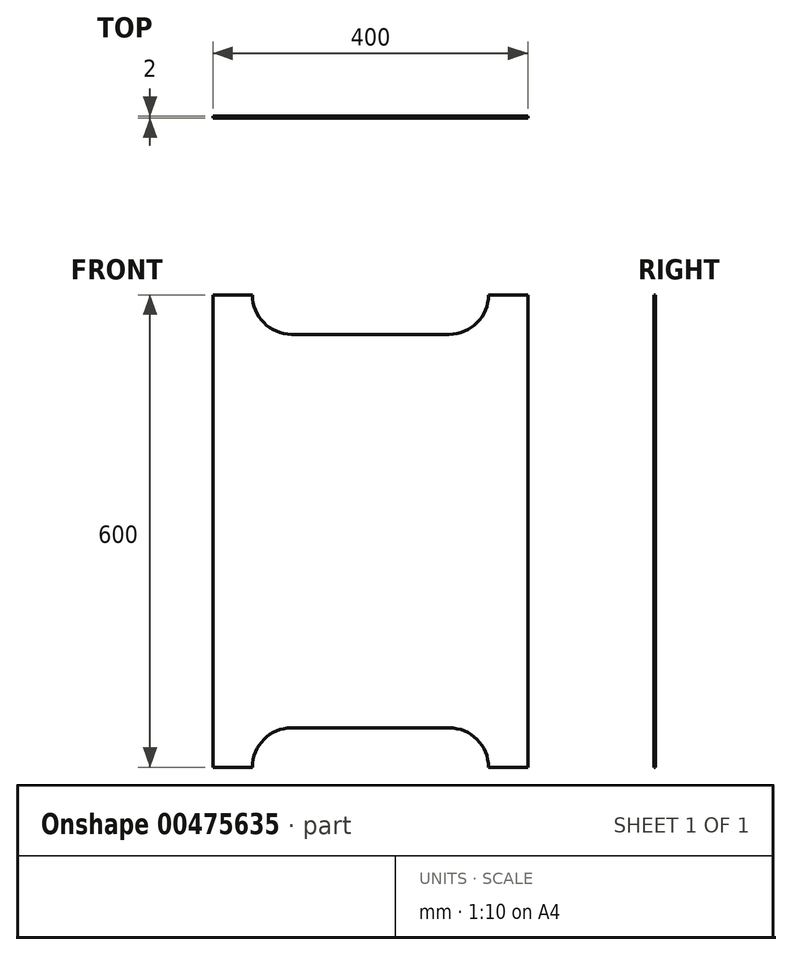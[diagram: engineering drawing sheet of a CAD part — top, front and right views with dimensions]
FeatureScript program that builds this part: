
annotation { "Feature Type Name" : "Feature", "Feature Type Description" : "" }
export const myFeature = defineFeature(function(context is Context, id is Id, definition is map)
    precondition{}
    {
        {
            var Q0;
            Q0=qCreatedBy(makeId("Front.planeOp"),FACE);
            var sketch = newSketch(context, id + "F0", { "sketchPlane" : qUnion([Q0])});
            skLineSegment(sketch, "E0.bottom", {"start": v(-200, 300) * mm, "end": v(-150, 300) * mm});
            skLineSegment(sketch, "E0.top", {"start": v(-200, -300) * mm, "end": v(-150, -300) * mm});
            skLineSegment(sketch, "E0.left", {"start": v(-200, 300) * mm, "end": v(-200, -300) * mm});
            skLineSegment(sketch, "E0.right", {"start": v(200, 300) * mm, "end": v(200, -300) * mm});
            skPoint(sketch, "E0.middle", {"position": v(0, 0) * mm});
            skLineSegment(sketch, "E1", {"start": v(-100, 250) * mm, "end": v(100, 250) * mm});
            skLineSegment(sketch, "E2", {"start": v(0, 250) * mm, "end": v(0, 300) * mm, "construction": true});
            skArc(sketch, "E3", {"start": v(100, 250) * mm, "mid": v(135.36, 264.64) * mm, "end": v(150, 300) * mm});
            skArc(sketch, "E4", {"start": v(-100, 250) * mm, "mid": v(-135.36, 264.64) * mm, "end": v(-150, 300) * mm});
            skLineSegment(sketch, "E5.trimOffspring", {"start": v(150, 300) * mm, "end": v(200, 300) * mm});
            skLineSegment(sketch, "E6.MirrorCS", {"start": v(-100, -250) * mm, "end": v(100, -250) * mm});
            skArc(sketch, "E7.MirrorCS", {"start": v(-100, -250) * mm, "mid": v(-135.36, -264.64) * mm, "end": v(-150, -300) * mm});
            skArc(sketch, "E8.MirrorCS", {"start": v(100, -250) * mm, "mid": v(135.36, -264.64) * mm, "end": v(150, -300) * mm});
            skLineSegment(sketch, "E9.trimOffspring", {"start": v(150, -300) * mm, "end": v(200, -300) * mm});
            skSolve(sketch);
        }
        {
            var Q0;
            Q0=makeQuery(id+"F0.imprint","IMPRINT",FACE,{"disambiguationData":[TD([[makeQuery(id+"F0.imprint","IMPRINT",EDGE,{"derivedFrom":sQuery(id+"F0.wireOp",EDGE,"E0.bottom")}),-1.0]])]});
            extrude(context, id + "F1", {"entities" : qUnion([Q0]), "endBound" : BoundingType.SYMMETRIC, "depth" : 2 * mm});
        }
    });
